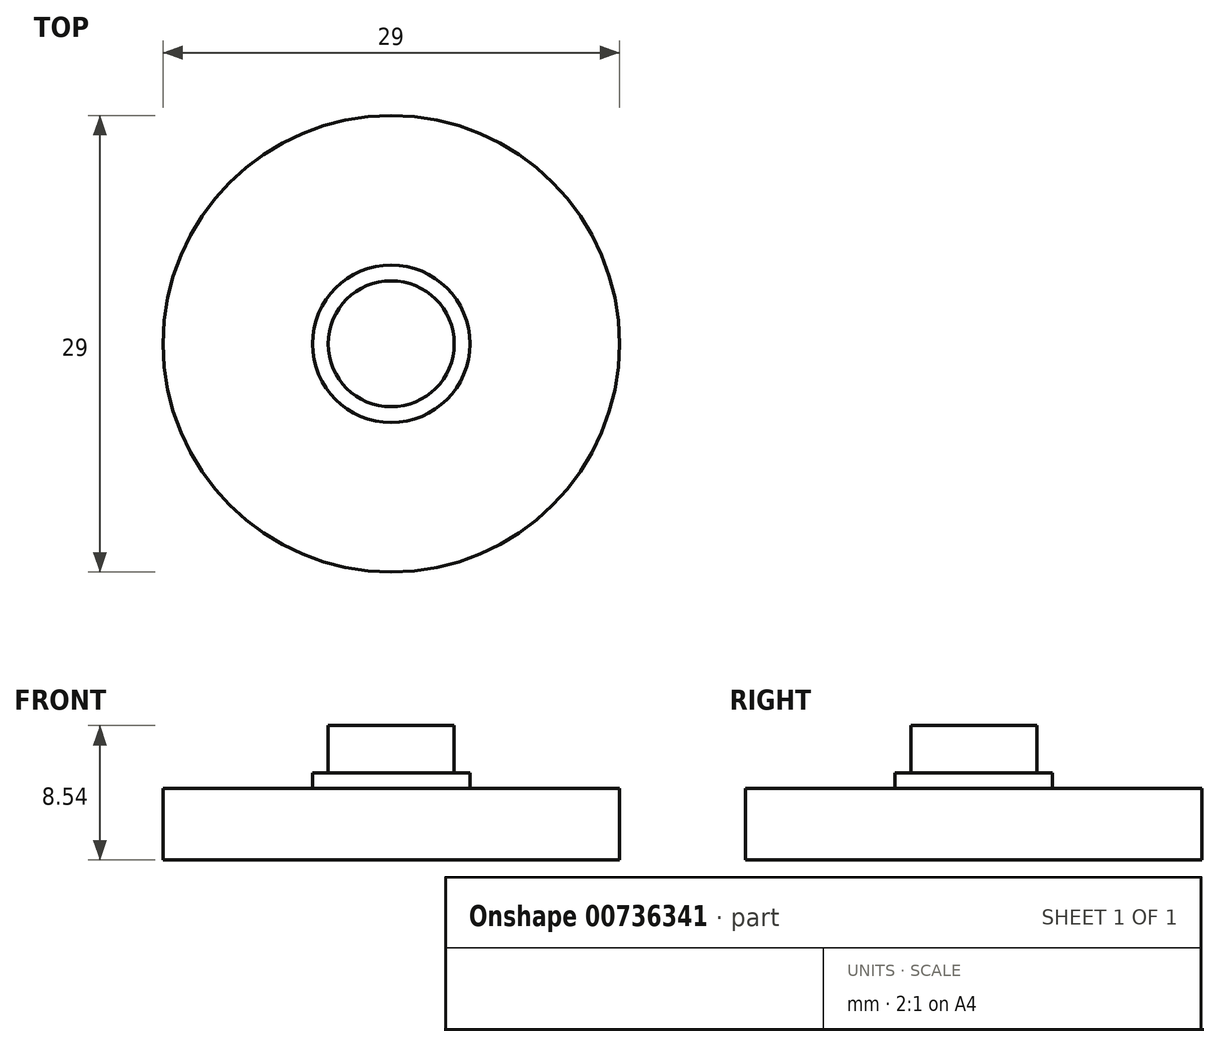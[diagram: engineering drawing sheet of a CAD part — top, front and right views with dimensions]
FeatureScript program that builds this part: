
annotation { "Feature Type Name" : "Feature", "Feature Type Description" : "" }
export const myFeature = defineFeature(function(context is Context, id is Id, definition is map)
    precondition{}
    {
        {
            var Q0;
            Q0=qCreatedBy(makeId("Top.planeOp"),FACE);
            var sketch = newSketch(context, id + "F0", { "sketchPlane" : qUnion([Q0])});
            skCircle(sketch, "E0", {"center": v(0, 0) * mm, "radius": 4 * mm});
            skSolve(sketch);
        }
        {
            var Q0;
            Q0=makeQuery(id+"F0.imprint","IMPRINT",FACE,{"disambiguationData":[TD([[makeQuery(id+"F0.imprint","IMPRINT",EDGE,{"derivedFrom":sQuery(id+"F0.wireOp",EDGE,"E0")}),1.0]])]});
            extrude(context, id + "F1", {"entities" : qUnion([Q0]), "depth" : 4 * mm, "offsetDistance" : 25.4 * mm});
        }
        {
            var Q0;
            Q0=qCreatedBy(makeId("Top.planeOp"),FACE);
            var sketch = newSketch(context, id + "F2", { "sketchPlane" : qUnion([Q0])});
            skCircle(sketch, "E1", {"center": v(0, 0) * mm, "radius": 14.5 * mm});
            skSolve(sketch);
        }
        {
            var Q0;
            Q0=makeQuery(id+"F2.imprint","IMPRINT",FACE,{"disambiguationData":[TD([[makeQuery(id+"F2.imprint","IMPRINT",EDGE,{"derivedFrom":sQuery(id+"F2.wireOp",EDGE,"E1")}),1.0]])]});
            extrude(context, id + "F3", {"entities" : qUnion([Q0]), "operationType" : NewBodyOperationType.ADD, "oppositeDirection" : true, "depth" : 2 * mm, "offsetDistance" : 25.4 * mm});
        }
        {
            var Q0;
            Q0=qCreatedBy(makeId("Top.planeOp"),FACE);
            var sketch = newSketch(context, id + "F4", { "sketchPlane" : qUnion([Q0])});
            skCircle(sketch, "E2", {"center": v(0, 0) * mm, "radius": 5 * mm});
            skSolve(sketch);
        }
        {
            var Q0;
            Q0=makeQuery(id+"F4.imprint","IMPRINT",FACE,{"disambiguationData":[TD([[makeQuery(id+"F4.imprint","IMPRINT",EDGE,{"derivedFrom":sQuery(id+"F4.wireOp",EDGE,"E2")}),1.0]])]});
            extrude(context, id + "F5", {"entities" : qUnion([Q0]), "operationType" : NewBodyOperationType.ADD, "depth" : 1 * mm, "offsetDistance" : 25.4 * mm});
        }
        {
            var Q0;
            Q0=makeQuery(id+"F3.opExtrude","CAP_FACE",FACE,{"disambiguationData":[OSD([sQuery(id+"F2.wireOp",EDGE,"E1")])],"isStart":false});
            extrude(context, id + "F6", {"entities" : qUnion([Q0]), "operationType" : NewBodyOperationType.ADD, "depth" : 2.54 * mm, "offsetDistance" : 25.4 * mm});
        }
    });
